# Revit family: LAMP_KOMBIC 200 RD
name_source: partatom
category: Luminarias
revit_build: Autodesk Revit 2018 (Build: 20190510_1515(x64)
units: mm (PartAtom-declared; Revit-internal decimal feet)

## family parameters
Anfitrión = Techo
Compartido = No
Corte con vacíos al cargar = No
Cota de conector redondo = Diámetro de uso
Número OmniClass = 23.80.70.11
Origen de luz = Sí
Punto de cálculo de habitación = No
Siempre vertical = Sí
Tipo de pieza = Normal
Título OmniClass = Luminaries for Internal Lighting

## types (12) — shared parameters
Altura central = 62 mm  [stored 0.203412 ft]
Altura exterior = 106 mm  [stored 0.347769 ft]
CRI = 80
Cambio de temperatura de color de luz atenuada = <Ninguno>
Comentarios de tipo = Availability of switching between accessories through visibility parameters when placed in a project.
Diam. exterior cuerpo = 167 mm  [stored 0.5479 ft]
Diam. inferior cuerpo = 220 mm  [stored 0.721785 ft]
Diam. inferior interior = 188 mm  [stored 0.616798 ft]
Diameter = 220 mm  [stored 0.721785 ft]
Fabricante = LAMP
Filtro de color = 16777215
Finish = RAL9010
Gear = Electronic
Height = 106 mm  [stored 0.347769 ft]
IEE = A+
Installation instructions = https://www.lamp.es
Insulation class = II
Last update = 22/02/2022
MacAdam = 3
Manufacturer URL = http://www.lamp.es
Manufacturer country = Spain
Manufacturer name = LAMP
Material Armazón BL = LAMP_PC Armazón Kombic BL
Material Armazón GR = LAMP_PC Armazón Kombic GR
Material Difusor = LAMP_PMMA Difusor Kombic
Material Disipador = LAMP_Aluminio Disipador Kombic
Model explanation = Availability of switching between accessories through visibility parameters when placed in a project.
Photobiological risk = Group 0
Power Supply = 220-240V 50/60Hz
Product URL = https://www.lamp.es
Product datasheet = http://www.lamp.es
Recessed diameter = 209 mm  [stored 0.685696 ft]
Ángulo de inclinación = 90.00°

## per-type parameters (varying)
| type | Archivo de red fotométrica | Descripción | Efficacy | LED Lifetime | Lámpara | Material Reflector | Modelo | Plum | Power | Product code | Protection rating | Type | Weight |
| 1982LM 3000 MATT BLANCO | K31RD3040OP830NMW.IES | KOMBIC 200 RD 3000 IP44 WW OPAL MA/WH | 110 lm/W | 50.000 L80 B10 | COB LED | LAMP_PC Reflector Kombic Metalizado Mate | K31RD3040OP830NMW | 18 W | 17 W | K31RD3040OP830NMW | IP2044 | COB TRIDONIC | 0.98 kg |
| 2065LM 3000 BRIGHT BLANCO | K31RD3040OP830NRW.IES | KOMBIC 200 RD 3000 IP44 WW BR/WH | 114 lm/W | 50.000 L80 B10 | MID-POWER LED | LAMP_PC Reflector Kombic Metalizado Brillante | K31RD3040OP830NRW | 18 W | 17 W | K31RD3040OP830NRW | IP2044 | MID POWER TRIDONIC | 0.98 kg |
| 2084LM 4000 MATT BLANCO | K31RD3040OP840NMW.IES | KOMBIC 200 RD 3000 IP44 NW MA/WH | 115 lm/W | 50.000 L80 B10 | COB LED | LAMP_PC Reflector Kombic Metalizado Mate | K31RD3040OP840NMW | 18 W | 17 W | K31RD3040OP840NMW | IP2044 | COB TRIDONIC | 0.98 kg |
| 2171LM 4000 BRIGHT BLANCO | K31RD3040OP840NRW.IES | KOMBIC 200 RD 3000 IP44 NW BR/WH | 120 lm/W | 50.000 L80 B10 | MID-POWER LED | LAMP_PC Reflector Kombic Metalizado Brillante | K31RD3040OP840NRW | 18 W | 17 W | K31RD3040OP840NRW | IP2044 | MID POWER TRIDONIC | 0.98 kg |
| 2688LM 3000 MATT BLANCO | K31RD4040OP830NMW.IES | KOMBIC 200 RD 4000 IP44 WW OPAL MA/WH | 106 lm/W | 50.000 L80 B10 | COB LED | LAMP_PC Reflector Kombic Metalizado Mate | K31RD4040OP830NMW | 25 W | 24 W | K31RD4040OP830NMW | IP44 | COB TRIDONIC | 0.98 kg |
| 2800LM 3000 BRIGHT BLANCO | K31RD4040OP830NRW.IES | KOMBIC 200 RD 4000 IP44 WW OPAL BR/WH | 110 lm/W | 50.000 L80 B10 | MID-POWER LED | LAMP_PC Reflector Kombic Metalizado Brillante | K31RD4040OP830NRW | 25 W | 24 W | K31RD4040OP830NRW | IP44 | MID POWER TRIDONIC | 0.98 kg |
| 2826LM 4000 MATT BLANCO | K31RD4040OP840NMW.IES | KOMBIC 200 RD 4000 IP44 NW OPAL MA/WH | 111 lm/W | 50.000 L80 B10 | COB LED | LAMP_PC Reflector Kombic Metalizado Mate | K31RD4040OP840NMW | 25 W | 24 W | K31RD4040OP840NMW | IP44 | COB TRIDONIC | 0.98 kg |
| 2944LM 4000 BRIGHT BLANCO | K31RD4040OP840NRW.IES | KOMBIC 200 RD 4000 IP44 NW OPAL BR/WH | 116 lm/W | 50.000 L80 B10 | MID-POWER LED | LAMP_PC Reflector Kombic Metalizado Brillante | K31RD4040OP840NRW | 25 W | 24 W | K31RD4040OP840NRW | IP44 | MID POWER TRIDONIC | 0.98 kg |
| 3576LM 3000 MATT BLANCO | K31RD5040OP830NMW.IES | KOMBIC 200 RD 5000 IP44 WW OPAL MA/WH | 94 lm/W | 50.000 L70 B10 | COB LED | LAMP_PC Reflector Kombic Metalizado Mate | K31RD5040OP830NMW | 38 W | 36 W | K31RD5040OP830NMW | IP44 | COB PHILIPS | 1.54 kg |
| 3735LM 3000 BRIGHT BLANCO | K31RD5040OP830NRW.IES | KOMBIC 200 RD 5000 IP44 WW OPAL BR/WH | 98 lm/W | 50.000 L70 B10 | COB LED | LAMP_PC Reflector Kombic Metalizado Brillante | K31RD5040OP830NRW | 38 W | 36 W | K31RD5040OP830NRW | IP44 | COB PHILIPS | 1.54 kg |
| 3845LM 4000 MATT BLANCO | K31RD5040OP840NMW.IES | KOMBIC 200 RD 5000 IP44 NW OPAL MA/WH | 101 lm/W | 50.000 L70 B10 | COB LED | LAMP_PC Reflector Kombic Metalizado Mate | K31RD5040OP840NMW | 38 W | 36 W | K31RD5040OP840NMW | IP44 | COB PHILIPS | 1.54 kg |
| 4016LM 4000 BRIGHT BLANCO | K31RD5040OP840NRW.IES | KOMBIC 200 RD 5000 IP44 NW OPAL BR/WH | 105 lm/W | 50.000 L70 B10 | COB LED | LAMP_PC Reflector Kombic Metalizado Brillante | K31RD5040OP840NRW | 38 W | 36 W | K31RD5040OP840NRW | IP44 | COB PHILIPS | 1.54 kg |

note: [stored X ft] marks values corroborated as IEEE doubles in the binary element streams (Revit-internal decimal feet)

## geometry (parser evidence)
native form markers: Blend x2
no freeform markers — native parametric forms only
